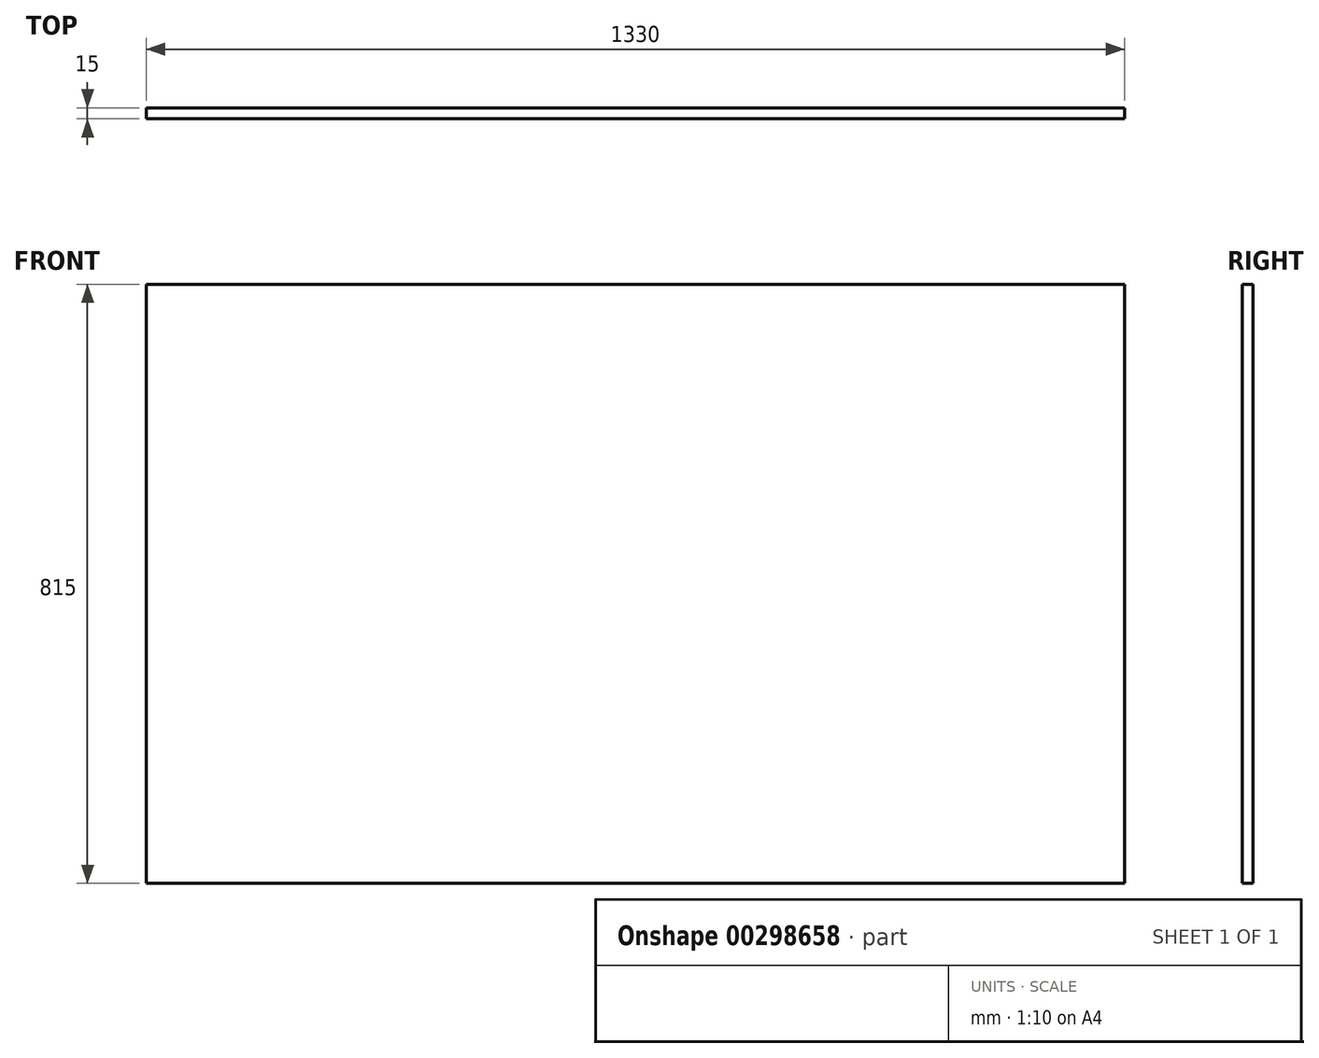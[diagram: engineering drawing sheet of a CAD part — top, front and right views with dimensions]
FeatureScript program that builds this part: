
annotation { "Feature Type Name" : "Feature", "Feature Type Description" : "" }
export const myFeature = defineFeature(function(context is Context, id is Id, definition is map)
    precondition{}
    {
        {
            var Q0;
            Q0=qCreatedBy(makeId("Front.planeOp"),FACE);
            var sketch = newSketch(context, id + "F0", { "sketchPlane" : qUnion([Q0])});
            skLineSegment(sketch, "E0.bottom", {"start": v(0, 0) * mm, "end": v(1330, 0) * mm});
            skLineSegment(sketch, "E0.top", {"start": v(0, 815) * mm, "end": v(1330, 815) * mm});
            skLineSegment(sketch, "E0.left", {"start": v(0, 0) * mm, "end": v(0, 815) * mm});
            skLineSegment(sketch, "E0.right", {"start": v(1330, 0) * mm, "end": v(1330, 815) * mm});
            skSolve(sketch);
        }
        {
            var Q0;
            Q0 = qSketchRegion(id + "F0", true);
            extrude(context, id + "F1", {"entities" : qUnion([Q0]), "depth" : 15 * mm});
        }
    });
